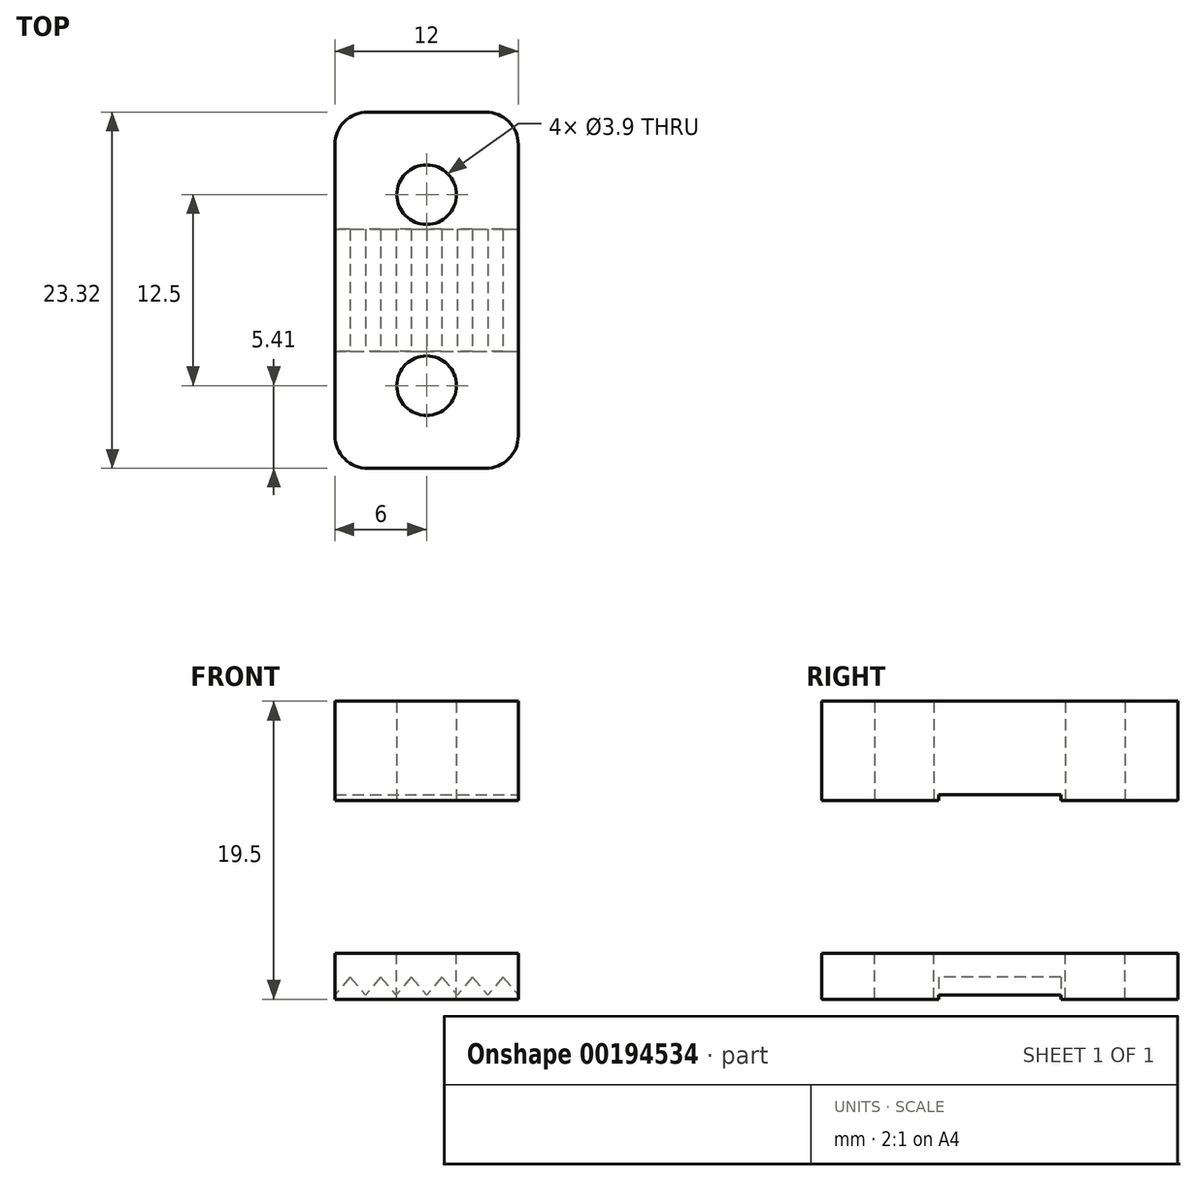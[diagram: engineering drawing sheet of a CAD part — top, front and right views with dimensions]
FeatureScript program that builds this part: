
annotation { "Feature Type Name" : "Feature", "Feature Type Description" : "" }
export const myFeature = defineFeature(function(context is Context, id is Id, definition is map)
    precondition{}
    {
        {
            var Q0;
            Q0=qCreatedBy(makeId("Top.planeOp"),FACE);
            var sketch = newSketch(context, id + "F0", { "sketchPlane" : qUnion([Q0])});
            skCircle(sketch, "E0", {"center": v(0, 6.25) * mm, "radius": 1.95 * mm});
            skLineSegment(sketch, "E1.bottom", {"start": v(-3.85, 11.66) * mm, "end": v(3.85, 11.66) * mm});
            skLineSegment(sketch, "E1.top", {"start": v(-6, 0) * mm, "end": v(6, 0) * mm});
            skLineSegment(sketch, "E1.left", {"start": v(-6, 9.52) * mm, "end": v(-6, 0) * mm});
            skLineSegment(sketch, "E1.right", {"start": v(6, 9.52) * mm, "end": v(6, 0) * mm});
            skPoint(sketch, "E2.visualSharp", {"position": v(-6, 11.66) * mm});
            skArc(sketch, "E2.filletArc", {"start": v(-3.85, 11.66) * mm, "mid": v(-5.37, 11.03) * mm, "end": v(-6, 9.52) * mm});
            skPoint(sketch, "E3.visualSharp", {"position": v(6, 11.66) * mm});
            skArc(sketch, "E3.filletArc", {"start": v(6, 9.52) * mm, "mid": v(5.37, 11.03) * mm, "end": v(3.85, 11.66) * mm});
            skSolve(sketch);
        }
        {
            var Q0;
            Q0=makeQuery(id+"F0.imprint","IMPRINT",FACE,{"disambiguationData":[TD([[makeQuery(id+"F0.imprint","IMPRINT",EDGE,{"derivedFrom":sQuery(id+"F0.wireOp",EDGE,"E0")}),-1.0]])]});
            extrude(context, id + "F1", {"entities" : qUnion([Q0]), "depth" : 6.5 * mm});
        }
        {
            var Q0;
            Q0=makeQuery(id+"F1.opExtrude","SWEPT_BODY",BODY,{"disambiguationData":[OSD([sQuery(id+"F0.wireOp",EDGE,"E0"),sQuery(id+"F0.wireOp",EDGE,"E1.bottom"),sQuery(id+"F0.wireOp",EDGE,"E1.top"),sQuery(id+"F0.wireOp",EDGE,"E1.left"),sQuery(id+"F0.wireOp",EDGE,"E1.right"),sQuery(id+"F0.wireOp",EDGE,"E2.filletArc"),sQuery(id+"F0.wireOp",EDGE,"E3.filletArc")])]});
            var Q1;
            Q1=qCreatedBy(makeId("Front.planeOp"),FACE);
            mirror(context, id + "F2", {"operationType" : NewBodyOperationType.ADD, "entities" : qUnion([Q0]), "mirrorPlane" : qUnion([Q1])});
        }
        {
            var Q0;
            Q0=qCreatedBy(makeId("Top.planeOp"),FACE);
            cPlane(context, id + "F3", {"entities" : qUnion([Q0]), "cplaneType" : CPlaneType.OFFSET, "offset" : 10 * mm, "oppositeDirection" : true, "width" : 150 * mm, "height" : 150 * mm});
        }
        {
            var Q0;
            Q0=qCreatedBy(id+"F3.planeOp",FACE);
            var sketch = newSketch(context, id + "F4", { "sketchPlane" : qUnion([Q0])});
            skCircle(sketch, "E4.0", {"center": v(0, -6.25) * mm, "radius": 1.95 * mm});
            skCircle(sketch, "E5.0", {"center": v(0, 6.25) * mm, "radius": 1.95 * mm});
            skLineSegment(sketch, "E6.0", {"start": v(-6, 9.52) * mm, "end": v(-6, -9.52) * mm});
            skArc(sketch, "E7.0", {"start": v(-3.85, -11.66) * mm, "mid": v(-5.37, -11.03) * mm, "end": v(-6, -9.52) * mm});
            skLineSegment(sketch, "E8.0", {"start": v(-3.85, -11.66) * mm, "end": v(3.85, -11.66) * mm});
            skPoint(sketch, "E9.0", {"position": v(5.37, -11.03) * mm});
            skArc(sketch, "E10.0", {"start": v(6, -9.52) * mm, "mid": v(5.37, -11.03) * mm, "end": v(3.85, -11.66) * mm});
            skLineSegment(sketch, "E11.0", {"start": v(6, 9.52) * mm, "end": v(6, -9.52) * mm});
            skArc(sketch, "E12.0", {"start": v(6, 9.52) * mm, "mid": v(5.37, 11.03) * mm, "end": v(3.85, 11.66) * mm});
            skLineSegment(sketch, "E13.0", {"start": v(-3.85, 11.66) * mm, "end": v(3.85, 11.66) * mm});
            skArc(sketch, "E14.0", {"start": v(-3.85, 11.66) * mm, "mid": v(-5.37, 11.03) * mm, "end": v(-6, 9.52) * mm});
            skSolve(sketch);
        }
        {
            var Q0;
            Q0=makeQuery(id+"F4.imprint","IMPRINT",FACE,{"disambiguationData":[TD([[makeQuery(id+"F4.imprint","IMPRINT",EDGE,{"derivedFrom":sQuery(id+"F4.wireOp",EDGE,"E4.0")}),-1.0]])]});
            extrude(context, id + "F5", {"entities" : qUnion([Q0]), "oppositeDirection" : true, "depth" : 3 * mm});
        }
        {
            var Q0;
            Q0=qCreatedBy(makeId("Front.planeOp"),FACE);
            var sketch = newSketch(context, id + "F6", { "sketchPlane" : qUnion([Q0])});
            skLineSegment(sketch, "E15.0", {"start": v(-6, -13) * mm, "end": v(-6, -12.73) * mm});
            skLineSegment(sketch, "E16.bottom", {"start": v(-6, -13) * mm, "end": v(-4, -13) * mm});
            skLineSegment(sketch, "E16.right", {"start": v(-4, -13) * mm, "end": v(-4, -12.73) * mm});
            skPoint(sketch, "E17", {"position": v(-5, -11.55) * mm});
            skLineSegment(sketch, "E18", {"start": v(-5, -11.55) * mm, "end": v(-4, -12.73) * mm});
            skLineSegment(sketch, "E19", {"start": v(-5, -11.55) * mm, "end": v(-6, -12.73) * mm});
            skPoint(sketch, "E20.orphan", {"position": v(-4, -11.55) * mm});
            skLineSegment(sketch, "E21.trimOffspring", {"start": v(-6, -11.55) * mm, "end": v(-6, -10) * mm});
            skLineSegment(sketch, "E22.1.0.0", {"start": v(-3, -11.55) * mm, "end": v(-2, -12.73) * mm});
            skLineSegment(sketch, "E22.1.0.1", {"start": v(-3, -11.55) * mm, "end": v(-4, -12.73) * mm});
            skLineSegment(sketch, "E22.1.0.3", {"start": v(-4, -13) * mm, "end": v(-2, -13) * mm});
            skLineSegment(sketch, "E22.1.0.4", {"start": v(-2, -13) * mm, "end": v(-2, -12.73) * mm});
            skLineSegment(sketch, "E22.2.0.0", {"start": v(-1, -11.55) * mm, "end": v(0, -12.73) * mm});
            skLineSegment(sketch, "E22.2.0.1", {"start": v(-1, -11.55) * mm, "end": v(-2, -12.73) * mm});
            skLineSegment(sketch, "E22.2.0.2", {"start": v(-2, -13) * mm, "end": v(-2, -12.73) * mm});
            skLineSegment(sketch, "E22.2.0.3", {"start": v(-2, -13) * mm, "end": v(0, -13) * mm});
            skLineSegment(sketch, "E22.2.0.4", {"start": v(0, -13) * mm, "end": v(0, -12.73) * mm});
            skLineSegment(sketch, "E22.3.0.0", {"start": v(1, -11.55) * mm, "end": v(2, -12.73) * mm});
            skLineSegment(sketch, "E22.3.0.1", {"start": v(1, -11.55) * mm, "end": v(0, -12.73) * mm});
            skLineSegment(sketch, "E22.3.0.2", {"start": v(0, -13) * mm, "end": v(0, -12.73) * mm});
            skLineSegment(sketch, "E22.3.0.3", {"start": v(0, -13) * mm, "end": v(2, -13) * mm});
            skLineSegment(sketch, "E22.3.0.4", {"start": v(2, -13) * mm, "end": v(2, -12.73) * mm});
            skLineSegment(sketch, "E22.4.0.0", {"start": v(3, -11.55) * mm, "end": v(4, -12.73) * mm});
            skLineSegment(sketch, "E22.4.0.1", {"start": v(3, -11.55) * mm, "end": v(2, -12.73) * mm});
            skLineSegment(sketch, "E22.4.0.2", {"start": v(2, -13) * mm, "end": v(2, -12.73) * mm});
            skLineSegment(sketch, "E22.4.0.3", {"start": v(2, -13) * mm, "end": v(4, -13) * mm});
            skLineSegment(sketch, "E22.4.0.4", {"start": v(4, -13) * mm, "end": v(4, -12.73) * mm});
            skLineSegment(sketch, "E22.5.0.0", {"start": v(5, -11.55) * mm, "end": v(6, -12.73) * mm});
            skLineSegment(sketch, "E22.5.0.1", {"start": v(5, -11.55) * mm, "end": v(4, -12.73) * mm});
            skLineSegment(sketch, "E22.5.0.2", {"start": v(4, -13) * mm, "end": v(4, -12.73) * mm});
            skLineSegment(sketch, "E22.5.0.3", {"start": v(4, -13) * mm, "end": v(6, -13) * mm});
            skLineSegment(sketch, "E22.5.0.4", {"start": v(6, -13) * mm, "end": v(6, -12.73) * mm});
            skLineSegment(sketch, "E22.direction1", {"start": v(-4, -12.73) * mm, "end": v(-2, -12.73) * mm, "construction": true});
            skSolve(sketch);
        }
        {
            var Q0;
            Q0 = qSketchRegion(id + "F6", true);
            extrude(context, id + "F7", {"entities" : qUnion([Q0]), "operationType" : NewBodyOperationType.REMOVE, "oppositeDirection" : true, "depth" : 4 * mm, "hasSecondDirection" : true, "secondDirectionOppositeDirection" : false, "secondDirectionDepth" : 4 * mm});
        }
        {
            var Q0;
            Q0=qCreatedBy(makeId("Top.planeOp"),FACE);
            var sketch = newSketch(context, id + "F8", { "sketchPlane" : qUnion([Q0])});
            skLineSegment(sketch, "E23.0", {"start": v(-6, 9.52) * mm, "end": v(-6, -9.52) * mm});
            skLineSegment(sketch, "E24.0", {"start": v(6, 9.52) * mm, "end": v(6, -9.52) * mm});
            skLineSegment(sketch, "E25.bottom", {"start": v(-6, 4) * mm, "end": v(6, 4) * mm});
            skLineSegment(sketch, "E25.top", {"start": v(-6, 0) * mm, "end": v(6, 0) * mm});
            skLineSegment(sketch, "E25.left", {"start": v(-6, 4) * mm, "end": v(-6, 0) * mm});
            skLineSegment(sketch, "E25.right", {"start": v(6, 4) * mm, "end": v(6, 0) * mm});
            skLineSegment(sketch, "E26.MirrorCS", {"start": v(-6, -4) * mm, "end": v(6, -4) * mm});
            skSolve(sketch);
        }
        {
            var Q0;
            Q0=makeQuery(id+"F8.imprint","IMPRINT",FACE,{"disambiguationData":[TD([[makeQuery(id+"F8.imprint","IMPRINT",EDGE,{"derivedFrom":sQuery(id+"F8.wireOp",EDGE,"E25.bottom")}),-1.0]])]});
            var Q1;
            {var subQ0=sQuery(id+"F8.wireOp",EDGE,"E25.top");Q1=makeQuery(id+"F8.imprint","IMPRINT",FACE,{"disambiguationData":[TD([[makeQuery(id+"F8.imprint","IMPRINT",EDGE,{"derivedFrom":subQ0}),-1.0]])]});}
            extrude(context, id + "F9", {"entities" : qUnion([Q0, Q1]), "operationType" : NewBodyOperationType.REMOVE, "depth" : 0.4 * mm});
        }
    });
